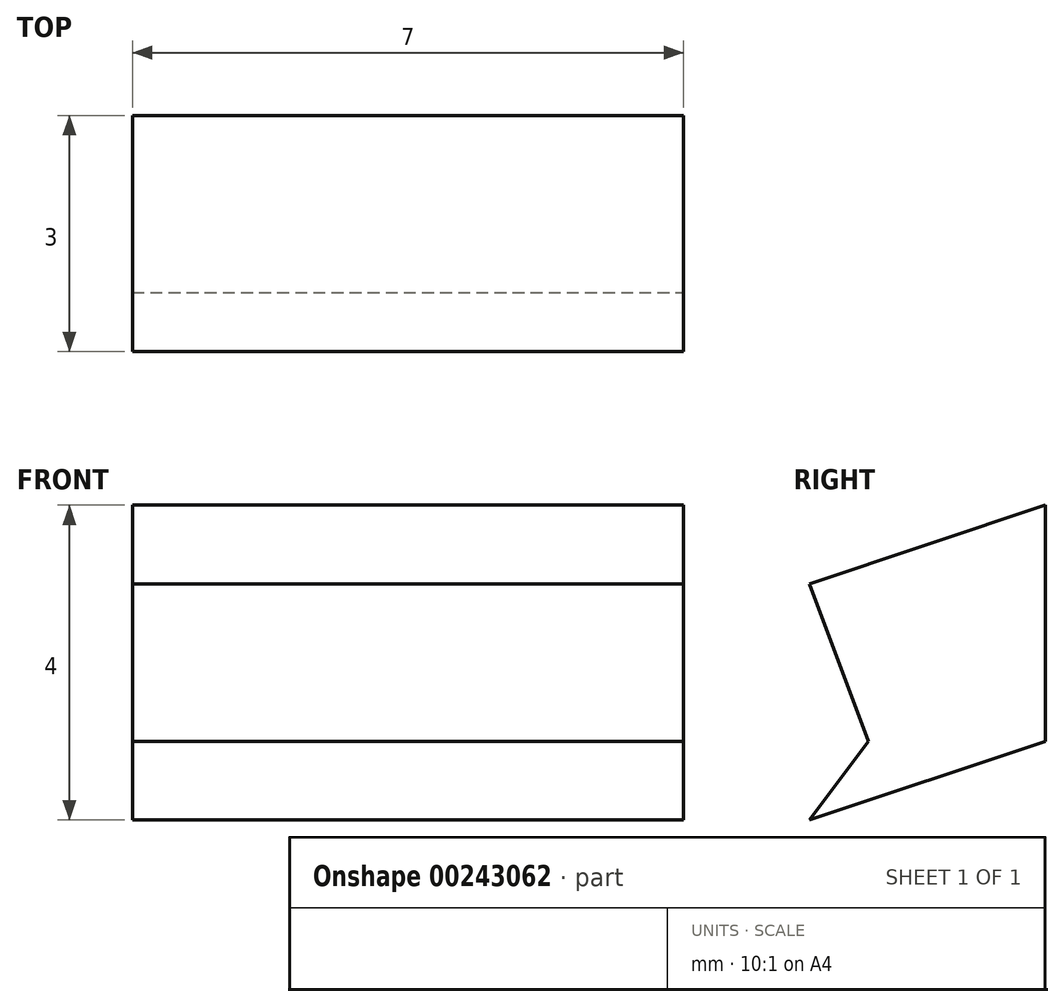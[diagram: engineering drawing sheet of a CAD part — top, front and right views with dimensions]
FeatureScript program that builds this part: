
annotation { "Feature Type Name" : "Feature", "Feature Type Description" : "" }
export const myFeature = defineFeature(function(context is Context, id is Id, definition is map)
    precondition{}
    {
        {
            var Q0;
            Q0=qCreatedBy(makeId("Top.planeOp"),FACE);
            var sketch = newSketch(context, id + "F0", { "sketchPlane" : qUnion([Q0])});
            skLineSegment(sketch, "E0.bottom", {"start": v(0, 0) * mm, "end": v(7, 0) * mm});
            skLineSegment(sketch, "E0.top", {"start": v(0, 3) * mm, "end": v(7, 3) * mm});
            skLineSegment(sketch, "E0.left", {"start": v(0, 0) * mm, "end": v(0, 3) * mm});
            skLineSegment(sketch, "E0.right", {"start": v(7, 0) * mm, "end": v(7, 3) * mm});
            skSolve(sketch);
        }
        {
            var Q0;
            Q0 = qSketchRegion(id + "F0", true);
            extrude(context, id + "F1", {"entities" : qUnion([Q0]), "depth" : 4 * mm});
        }
        {
            var Q0;
            Q0=makeQuery(id+"F1.opExtrude","SWEPT_FACE",FACE,{"disambiguationData":[OSD([sQuery(id+"F0.wireOp",EDGE,"E0.right")])]});
            var sketch = newSketch(context, id + "F2", { "sketchPlane" : qUnion([Q0])});
            skLineSegment(sketch, "E1", {"start": v(0, 0) * mm, "end": v(3, 1) * mm});
            skLineSegment(sketch, "E2", {"start": v(0, 0) * mm, "end": v(0, 3) * mm});
            skLineSegment(sketch, "E3", {"start": v(0, 0) * mm, "end": v(3, 4) * mm});
            skLineSegment(sketch, "E4", {"start": v(0, 0) * mm, "end": v(0.75, 1) * mm});
            skLineSegment(sketch, "E5", {"start": v(0.75, 1) * mm, "end": v(0.75, 0) * mm, "construction": true});
            skLineSegment(sketch, "E6", {"start": v(0, 3) * mm, "end": v(0.75, 1) * mm});
            skLineSegment(sketch, "E7", {"start": v(0, 3) * mm, "end": v(3, 4) * mm});
            skLineSegment(sketch, "E8", {"start": v(0, 4) * mm, "end": v(3, 4) * mm});
            skLineSegment(sketch, "E9", {"start": v(0, 4) * mm, "end": v(0, 3) * mm});
            skSolve(sketch);
        }
        {
            var Q0;
            Q0=makeQuery(id+"F2.imprint","IMPRINT",FACE,{"disambiguationData":[TD([[makeQuery(id+"F2.imprint","IMPRINT",EDGE,{"derivedFrom":sQuery(id+"F2.wireOp",EDGE,"E7")}),1.0]])]});
            var Q1;
            Q1=makeQuery(id+"F2.imprint","IMPRINT",FACE,{"disambiguationData":[TD([[makeQuery(id+"F2.imprint","IMPRINT",EDGE,{"derivedFrom":sQuery(id+"F2.wireOp",EDGE,"E2")}),1.0]])]});
            var Q2;
            {var subQ0=sQuery(id+"F2.wireOp",EDGE,"E1");Q2=makeQuery(id+"F2.imprint","IMPRINT",FACE,{"disambiguationData":[TD([[makeQuery(id+"F2.imprint","IMPRINT",EDGE,{"derivedFrom":subQ0}),-1.0]])]});}
            extrude(context, id + "F3", {"entities" : qUnion([Q0, Q1, Q2]), "operationType" : NewBodyOperationType.REMOVE, "oppositeDirection" : true, "depth" : 25 * mm});
        }
    });
